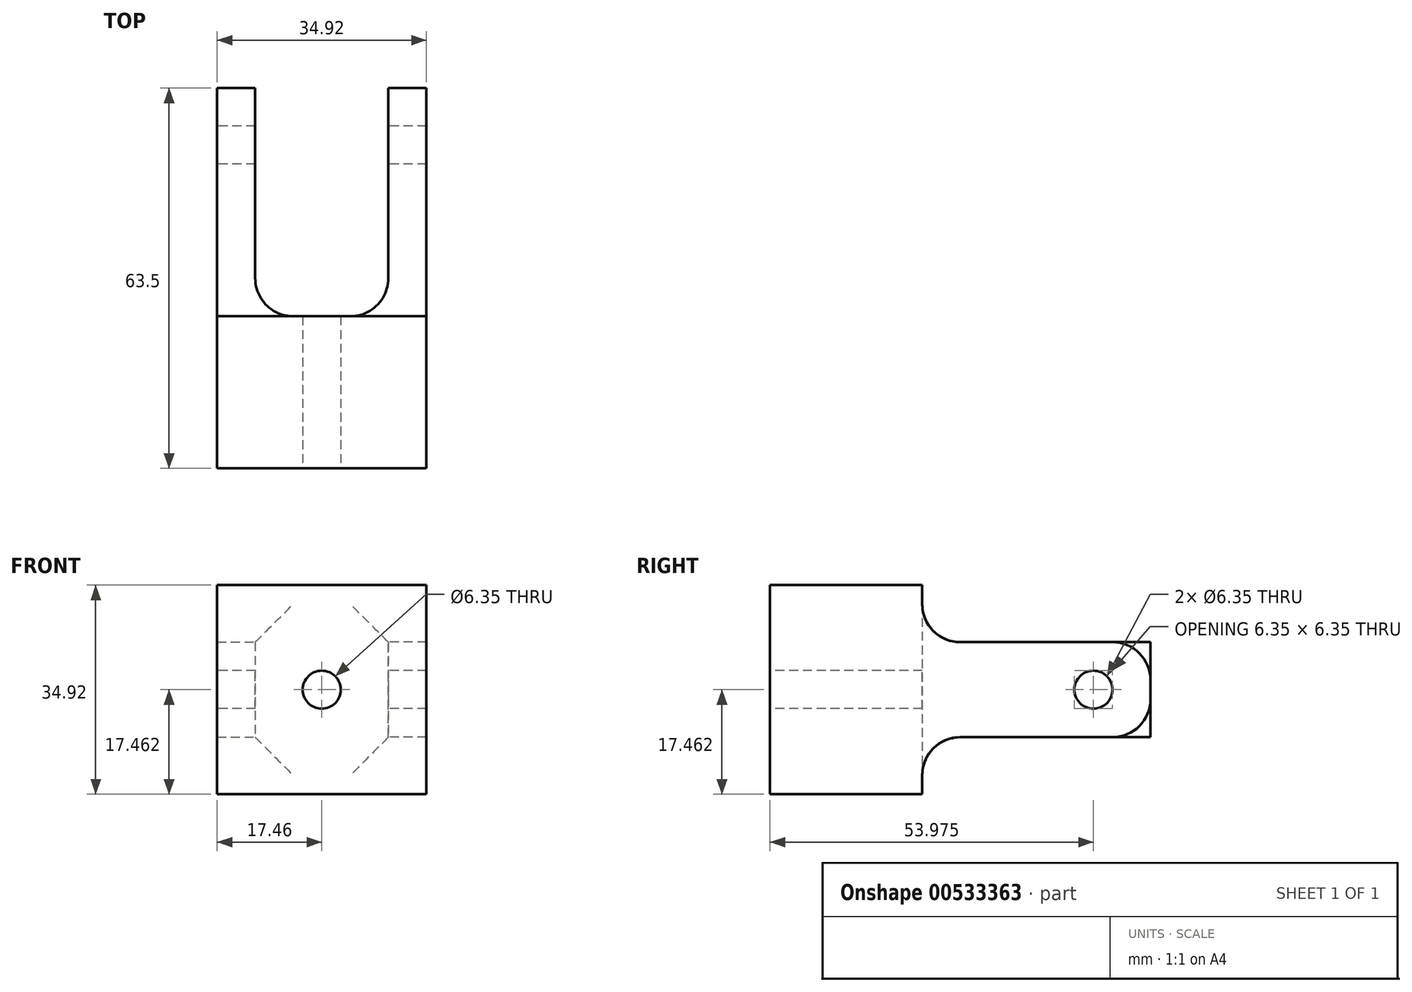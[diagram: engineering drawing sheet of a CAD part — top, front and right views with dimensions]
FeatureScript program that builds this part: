
annotation { "Feature Type Name" : "Feature", "Feature Type Description" : "" }
export const myFeature = defineFeature(function(context is Context, id is Id, definition is map)
    precondition{}
    {
        {
            var Q0;
            Q0=qCreatedBy(makeId("Top.planeOp"),FACE);
            var sketch = newSketch(context, id + "F0", { "sketchPlane" : qUnion([Q0])});
            skLineSegment(sketch, "E0.bottom", {"start": v(17.46, -31.75) * mm, "end": v(-17.46, -31.75) * mm});
            skLineSegment(sketch, "E0.top", {"start": v(17.46, 31.75) * mm, "end": v(-17.46, 31.75) * mm});
            skLineSegment(sketch, "E0.left", {"start": v(17.46, -31.75) * mm, "end": v(17.46, 31.75) * mm});
            skLineSegment(sketch, "E0.right", {"start": v(-17.46, -31.75) * mm, "end": v(-17.46, 31.75) * mm});
            skPoint(sketch, "E0.middle", {"position": v(0, 0) * mm});
            skSolve(sketch);
        }
        {
            var Q0;
            Q0 = qSketchRegion(id + "F0", true);
            extrude(context, id + "F1", {"entities" : qUnion([Q0]), "depth" : 34.92 * mm, "offsetDistance" : 25.4 * mm});
        }
        {
            var Q0;
            Q0=makeQuery(id+"F1.opExtrude","SWEPT_FACE",FACE,{"disambiguationData":[OSD([sQuery(id+"F0.wireOp",EDGE,"E0.top")])]});
            var sketch = newSketch(context, id + "F2", { "sketchPlane" : qUnion([Q0])});
            skLineSegment(sketch, "E1.bottom", {"start": v(-17.46, 34.93) * mm, "end": v(-11.11, 34.93) * mm});
            skLineSegment(sketch, "E1.top", {"start": v(-17.46, 0) * mm, "end": v(-11.11, 0) * mm});
            skLineSegment(sketch, "E1.left", {"start": v(-17.46, 34.93) * mm, "end": v(-17.46, 0) * mm});
            skLineSegment(sketch, "E1.right", {"start": v(-11.11, 34.93) * mm, "end": v(-11.11, 0) * mm});
            skLineSegment(sketch, "E2.MirrorCS", {"start": v(11.11, 34.93) * mm, "end": v(11.11, 0) * mm});
            skLineSegment(sketch, "E3.MirrorCS", {"start": v(17.46, 34.93) * mm, "end": v(11.11, 34.93) * mm});
            skLineSegment(sketch, "E4.MirrorCS", {"start": v(17.46, 34.93) * mm, "end": v(17.46, 0) * mm});
            skLineSegment(sketch, "E5.MirrorCS", {"start": v(17.46, 0) * mm, "end": v(11.11, 0) * mm});
            skLineSegment(sketch, "E6", {"start": v(-17.46, 25.4) * mm, "end": v(-11.11, 25.4) * mm});
            skLineSegment(sketch, "E7", {"start": v(-17.46, 9.53) * mm, "end": v(-11.11, 9.53) * mm});
            skLineSegment(sketch, "E8.MirrorCS", {"start": v(17.46, 25.4) * mm, "end": v(11.11, 25.4) * mm});
            skLineSegment(sketch, "E9.MirrorCS", {"start": v(17.46, 9.53) * mm, "end": v(11.11, 9.53) * mm});
            skSolve(sketch);
        }
        {
            var Q0;
            {var subQ0=sQuery(id+"F2.wireOp",EDGE,"E1.bottom");Q0=makeQuery(id+"F2.imprint","IMPRINT",FACE,{"disambiguationData":[TD([[makeQuery(id+"F2.imprint","IMPRINT",EDGE,{"derivedFrom":subQ0}),-1.0]])]});}
            var Q1;
            {var subQ0=sQuery(id+"F2.wireOp",EDGE,"E1.top");Q1=makeQuery(id+"F2.imprint","IMPRINT",FACE,{"disambiguationData":[TD([[makeQuery(id+"F2.imprint","IMPRINT",EDGE,{"derivedFrom":subQ0}),1.0]])]});}
            var Q2;
            {var subQ0=sQuery(id+"F2.wireOp",EDGE,"E3.MirrorCS");Q2=makeQuery(id+"F2.imprint","IMPRINT",FACE,{"disambiguationData":[TD([[makeQuery(id+"F2.imprint","IMPRINT",EDGE,{"derivedFrom":subQ0}),-1.0]])]});}
            var Q3;
            {var subQ0=sQuery(id+"F2.wireOp",EDGE,"E5.MirrorCS");Q3=makeQuery(id+"F2.imprint","IMPRINT",FACE,{"disambiguationData":[TD([[makeQuery(id+"F2.imprint","IMPRINT",EDGE,{"derivedFrom":subQ0}),1.0]])]});}
            var Q4;
            {var subQ5=sQuery(id+"F2.wireOp",EDGE,"E1.right");var subQ9=makeQuery(id+"F2.imprint","INTERSECT",VERTEX,{"derivedFrom":[subQ5,sQuery(id+"F2.wireOp",EDGE,"E6")]});Q4=makeQuery(id+"F2.imprint","IMPRINT",FACE,{"disambiguationData":[TD([[makeQuery(id+"F2.imprint","IMPRINT",EDGE,{"disambiguationData":[TD([[subQ9,-1.0]])],"derivedFrom":subQ5}),1.0]])]});}
            extrude(context, id + "F3", {"entities" : qUnion([Q0, Q1, Q2, Q3, Q4]), "operationType" : NewBodyOperationType.REMOVE, "oppositeDirection" : true, "depth" : 38.1 * mm, "offsetDistance" : 25.4 * mm});
        }
        {
            var Q0;
            Q0=makeQuery(id+"F1.opExtrude","SWEPT_FACE",FACE,{"disambiguationData":[OSD([sQuery(id+"F0.wireOp",EDGE,"E0.right")])]});
            var sketch = newSketch(context, id + "F4", { "sketchPlane" : qUnion([Q0])});
            skCircle(sketch, "E10", {"center": v(-22.22, 17.46) * mm, "radius": 3.18 * mm});
            skPoint(sketch, "E10.centerSnap0", {"position": v(-31.75, 17.46) * mm});
            skSolve(sketch);
        }
        {
            var Q0;
            Q0 = qSketchRegion(id + "F4", true);
            extrude(context, id + "F5", {"entities" : qUnion([Q0]), "operationType" : NewBodyOperationType.REMOVE, "endBound" : BoundingType.THROUGH_ALL, "oppositeDirection" : true, "depth" : 25.4 * mm, "offsetDistance" : 25.4 * mm});
        }
        {
            var Q0;
            Q0=makeQuery(id+"F1.opExtrude","SWEPT_FACE",FACE,{"disambiguationData":[OSD([sQuery(id+"F0.wireOp",EDGE,"E0.bottom")])]});
            var sketch = newSketch(context, id + "F6", { "sketchPlane" : qUnion([Q0])});
            skCircle(sketch, "E11", {"center": v(0, 17.46) * mm, "radius": 3.18 * mm});
            skPoint(sketch, "E11.centerSnap0", {"position": v(17.46, 17.46) * mm});
            skSolve(sketch);
        }
        {
            var Q0;
            Q0 = qSketchRegion(id + "F6", true);
            extrude(context, id + "F7", {"entities" : qUnion([Q0]), "operationType" : NewBodyOperationType.REMOVE, "oppositeDirection" : true, "depth" : 25.4 * mm, "offsetDistance" : 25.4 * mm});
        }
        {
            var Q0;
            Q0=makeQuery(id+"F3.boolean.opBoolean","COPY",EDGE,{"derivedFrom":makeQuery(id+"F3.opExtrude","CAP_EDGE",EDGE,{"disambiguationData":[OSD([sQuery(id+"F2.wireOp",EDGE,"E6")])],"isStart":true})});
            var Q1;
            Q1=makeQuery(id+"F3.boolean.opBoolean","COPY",EDGE,{"derivedFrom":makeQuery(id+"F3.opExtrude","CAP_EDGE",EDGE,{"disambiguationData":[OSD([sQuery(id+"F2.wireOp",EDGE,"E6")])],"isStart":false})});
            var Q2;
            Q2=makeQuery(id+"F3.boolean.opBoolean","COPY",EDGE,{"derivedFrom":makeQuery(id+"F3.opExtrude","CAP_EDGE",EDGE,{"disambiguationData":[OSD([sQuery(id+"F2.wireOp",EDGE,"E8.MirrorCS")])],"isStart":false})});
            var Q3;
            Q3=makeQuery(id+"F3.boolean.opBoolean","COPY",EDGE,{"derivedFrom":makeQuery(id+"F3.opExtrude","CAP_EDGE",EDGE,{"disambiguationData":[OSD([sQuery(id+"F2.wireOp",EDGE,"E8.MirrorCS")])],"isStart":true})});
            var Q4;
            Q4=makeQuery(id+"F3.boolean.opBoolean","COPY",EDGE,{"derivedFrom":makeQuery(id+"F3.opExtrude","CAP_EDGE",EDGE,{"disambiguationData":[OSD([sQuery(id+"F2.wireOp",EDGE,"E9.MirrorCS")])],"isStart":true})});
            var Q5;
            Q5=makeQuery(id+"F3.boolean.opBoolean","COPY",EDGE,{"derivedFrom":makeQuery(id+"F3.opExtrude","CAP_EDGE",EDGE,{"disambiguationData":[OSD([sQuery(id+"F2.wireOp",EDGE,"E7")])],"isStart":true})});
            var Q6;
            Q6=makeQuery(id+"F3.boolean.opBoolean","COPY",EDGE,{"derivedFrom":makeQuery(id+"F3.opExtrude","CAP_EDGE",EDGE,{"disambiguationData":[OSD([sQuery(id+"F2.wireOp",EDGE,"E7")])],"isStart":false})});
            var Q7;
            Q7=makeQuery(id+"F3.boolean.opBoolean","COPY",EDGE,{"derivedFrom":makeQuery(id+"F3.opExtrude","CAP_EDGE",EDGE,{"disambiguationData":[OSD([sQuery(id+"F2.wireOp",EDGE,"E9.MirrorCS")])],"isStart":false})});
            var Q8;
            Q8=makeQuery(id+"F3.boolean.opBoolean","COPY",EDGE,{"derivedFrom":makeQuery(id+"F3.opExtrude","CAP_EDGE",EDGE,{"disambiguationData":[OSD([sQuery(id+"F2.wireOp",EDGE,"E1.right")])],"isStart":false})});
            var Q9;
            Q9=makeQuery(id+"F3.boolean.opBoolean","COPY",EDGE,{"derivedFrom":makeQuery(id+"F3.opExtrude","CAP_EDGE",EDGE,{"disambiguationData":[OSD([sQuery(id+"F2.wireOp",EDGE,"E2.MirrorCS")])],"isStart":false})});
            fillet(context, id + "F8", {"entities" : qUnion([Q0, Q1, Q2, Q3, Q4, Q5, Q6, Q7, Q8, Q9]), "radius" : 6.35 * mm, "tangentPropagation" : true, "allowEdgeOverflow" : false});
        }
    });
